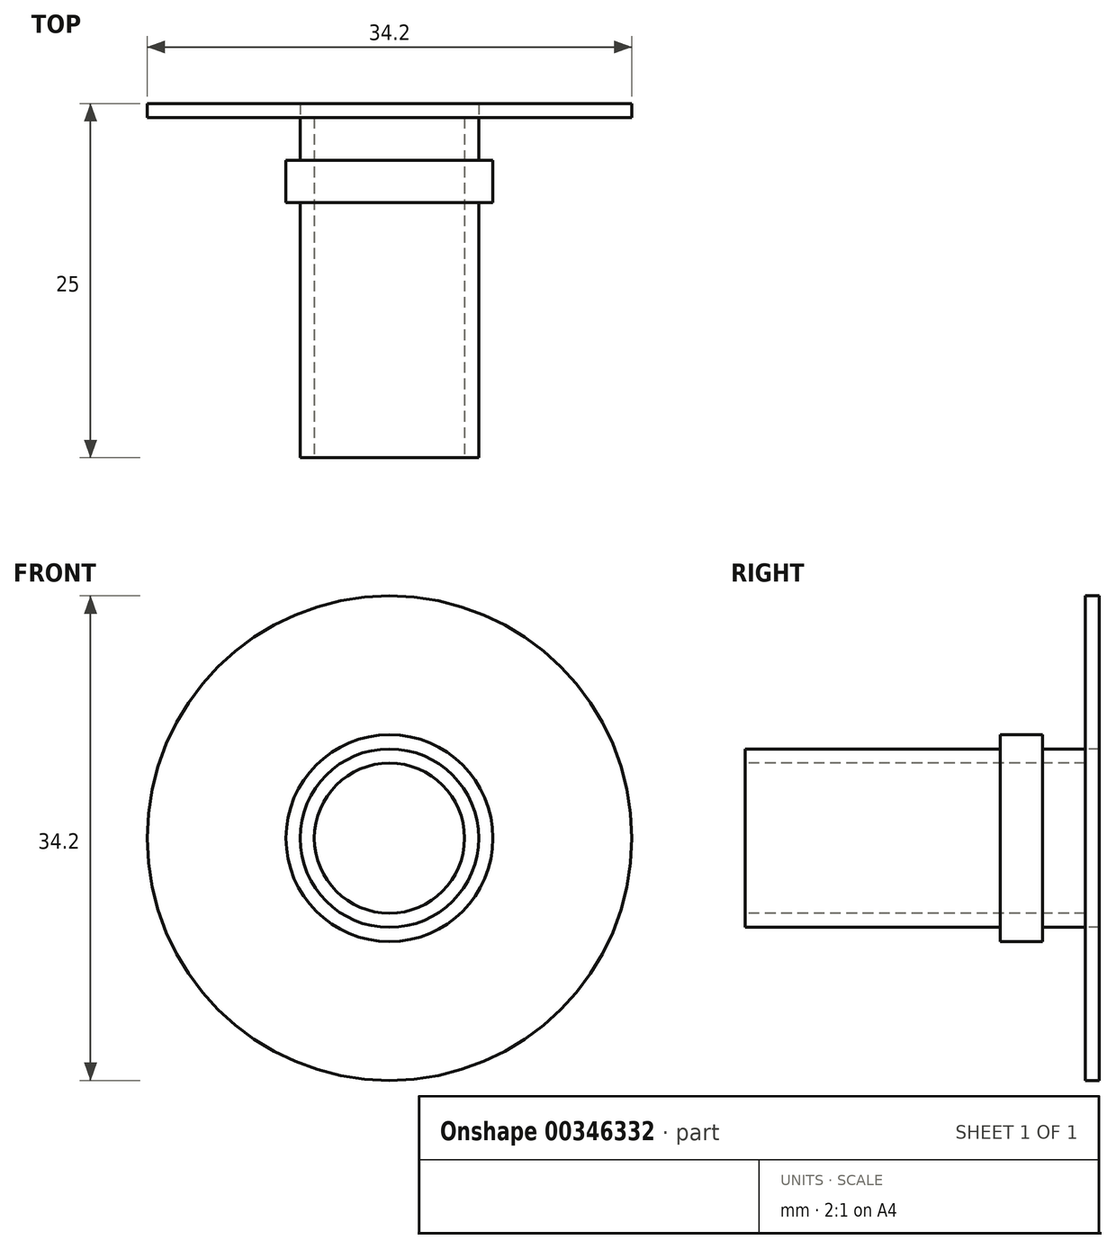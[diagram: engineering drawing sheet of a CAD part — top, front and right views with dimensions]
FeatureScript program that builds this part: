
annotation { "Feature Type Name" : "Feature", "Feature Type Description" : "" }
export const myFeature = defineFeature(function(context is Context, id is Id, definition is map)
    precondition{}
    {
        {
            var Q0;
            Q0=qCreatedBy(makeId("Top.planeOp"),FACE);
            var sketch = newSketch(context, id + "F0", { "sketchPlane" : qUnion([Q0])});
            skLineSegment(sketch, "E0", {"start": v(0, -33.43) * mm, "end": v(0, 43.44) * mm});
            skSolve(sketch);
        }
        {
            var Q0;
            Q0=qCreatedBy(makeId("Top.planeOp"),FACE);
            var sketch = newSketch(context, id + "F1", { "sketchPlane" : qUnion([Q0])});
            skLineSegment(sketch, "E1.bottom", {"start": v(5.3, -5.3) * mm, "end": v(6.3, -5.3) * mm});
            skLineSegment(sketch, "E1.top", {"start": v(5.3, 19.7) * mm, "end": v(6.3, 19.7) * mm});
            skLineSegment(sketch, "E1.left", {"start": v(5.3, -5.3) * mm, "end": v(5.3, 19.7) * mm});
            skLineSegment(sketch, "E1.right", {"start": v(6.3, -5.3) * mm, "end": v(6.3, 19.7) * mm});
            skLineSegment(sketch, "E2.bottom", {"start": v(5.3, 19.7) * mm, "end": v(17.1, 19.7) * mm});
            skLineSegment(sketch, "E2.top", {"start": v(5.3, 18.7) * mm, "end": v(17.1, 18.7) * mm});
            skLineSegment(sketch, "E2.left", {"start": v(5.3, 19.7) * mm, "end": v(5.3, 18.7) * mm});
            skLineSegment(sketch, "E2.right", {"start": v(17.1, 19.7) * mm, "end": v(17.1, 18.7) * mm});
            skLineSegment(sketch, "E3.bottom", {"start": v(6.3, 18.7) * mm, "end": v(7, 18.7) * mm});
            skLineSegment(sketch, "E3.top", {"start": v(6.3, 15.7) * mm, "end": v(7.3, 15.7) * mm});
            skLineSegment(sketch, "E3.left", {"start": v(6.3, 18.7) * mm, "end": v(6.3, 15.7) * mm});
            skArc(sketch, "E4", {"start": v(7, 18.7) * mm, "mid": v(6.49, 17.13) * mm, "end": v(7.3, 15.7) * mm});
            skLineSegment(sketch, "E5.top", {"start": v(6.3, 12.7) * mm, "end": v(7.3, 12.7) * mm});
            skLineSegment(sketch, "E5.left", {"start": v(6.3, 15.7) * mm, "end": v(6.3, 12.7) * mm});
            skLineSegment(sketch, "E5.right", {"start": v(7.3, 15.7) * mm, "end": v(7.3, 12.7) * mm});
            skSolve(sketch);
        }
        {
            var Q0;
            {var subQ5=sQuery(id+"F1.wireOp",EDGE,"E2.left");Q0=makeQuery(id+"F1.imprint","IMPRINT",FACE,{"disambiguationData":[TD([[makeQuery(id+"F1.imprint","IMPRINT",EDGE,{"derivedFrom":subQ5}),1.0]])]});}
            var Q1;
            {var subQ1=sQuery(id+"F1.wireOp",EDGE,"E1.bottom");Q1=makeQuery(id+"F1.imprint","IMPRINT",FACE,{"disambiguationData":[TD([[makeQuery(id+"F1.imprint","IMPRINT",EDGE,{"derivedFrom":subQ1}),1.0]])]});}
            var Q2;
            {var subQ0=sQuery(id+"F1.wireOp",EDGE,"E2.right");Q2=makeQuery(id+"F1.imprint","IMPRINT",FACE,{"disambiguationData":[TD([[makeQuery(id+"F1.imprint","IMPRINT",EDGE,{"derivedFrom":subQ0}),-1.0]])]});}
            var Q3;
            Q3=makeQuery(id+"F1.imprint","IMPRINT",FACE,{"disambiguationData":[TD([[makeQuery(id+"F1.imprint","IMPRINT",EDGE,{"derivedFrom":sQuery(id+"F1.wireOp",EDGE,"E3.bottom")}),-1.0]])]});
            var Q4;
            Q4=makeQuery(id+"F1.imprint","IMPRINT",FACE,{"disambiguationData":[TD([[makeQuery(id+"F1.imprint","IMPRINT",EDGE,{"derivedFrom":sQuery(id+"F1.wireOp",EDGE,"E3.top")}),-1.0]])]});
            var Q5;
            Q5=sQuery(id+"F0.wireOp",EDGE,"E0");
            revolve(context, id + "F2", {"entities" : qUnion([Q0, Q1, Q2, Q3, Q4]), "axis" : qUnion([Q5]), "revolveType" : RevolveType.FULL});
        }
    });
